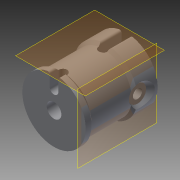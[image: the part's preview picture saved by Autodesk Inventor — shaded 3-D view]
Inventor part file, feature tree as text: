
AUTODESK INVENTOR PART (.ipt)
format: ipt  version: 2013 (Build 170138000, 138)  size: 317,952 bytes
history: native  units: in
note: dims shown in document units (in); Inventor stores cm internally (conversion verified against a paired STEP export)
features: extrude x13, sketch x13, pattern_circular x3, fillet x3, projected_geometry x3, chamfer x2, plane x2
ambient origin geometry x8: Origin, YZ Plane, XZ Plane, XY Plane, X Axis, Y Axis, Z Axis, Center Point
bodies: Solid1 (feature_tree)
feature tree (39):
  extrude  "Extrusion1"  Depth=0.9843in TaperAngle=0.0deg
  extrude  "Extrusion2"  Depth=0.315in TaperAngle=0.0deg
  extrude  "Extrusion3"  Depth=0.1181in TaperAngle=0.0deg
  chamfer  "Chamfer1"  Distance=0.0394in Angle=45.0deg
  extrude  "Extrusion4"  Depth=0.0984in
  extrude  "Extrusion5"  Depth=0.2008in
  plane  "Work Plane1"
  extrude  "Extrusion6"  Depth=0.1181in
  extrude  "Extrusion7"  Depth=0.1181in
  extrude  "Extrusion8"  Depth=0.1181in TaperAngle=0.0deg
  chamfer  "Chamfer2"  Distance=0.1181in
  extrude  "Extrusion9"  Depth=0.1575in
  extrude  "Extrusion10"  Depth=0.0394in
  pattern_circular  "Circular Pattern1"  Count=2 Angle=360.0deg
  fillet  "Fillet1"  Radius=0.0295in
  plane  "Work Plane2"
  extrude  "Extrusion15"  Depth=1.0in TaperAngle=0.0deg
  pattern_circular  "Circular Pattern3"  Angle=45.0deg  [1 undecoded]
  fillet  "Fillet3"  Radius=0.7874in
  extrude  "Extrusion11"  Depth=0.0394in
  extrude  "Extrusion14"  Depth=0.374in
  pattern_circular  "Circular Pattern2"  [2 undecoded]
  fillet  "Fillet2"  Radius=1.0in
  sketch  "Sketch1"  dims[d0=0.7874in d2=0.9843in d3=0.0in]
  sketch  "Sketch2"  dims[d4=0.0394in d5=0.315in d6=0.0in]
  sketch  "Sketch3"  dims[d7=0.0394in d8=0.1181in d9=0.0in d10=0.0394in d11=0.125in d12=45.0deg]
  sketch  "Sketch4"  dims[d14=0.126in d17=0.0984in]
  sketch  "Sketch5"  dims[d18=0.1181in d19=0.0in d20=0.2008in]
  sketch  "Sketch6"  dims[d22=0.2461in d23=0.1181in]
  projected_geometry  "Projected Loop1"
  sketch  "Sketch7"  dims[d24=0.1181in d25=0.0in d26=0.1181in]
  sketch  "Sketch8"  dims[d29=0.1181in d30=0.0in d31=0.1181in d32=0.0in d33=0.1181in d34=0.0in]
  sketch  "Sketch9"  dims[d35=0.0394in d36=0.125in d37=45.0deg d38=0.1575in]
  sketch  "Sketch10"  dims[d40=0.2205in d41=0.0394in]
  sketch  "Sketch11"  dims[d42=0.2165in d43=0.0in]
  sketch  "Sketch14"  dims[d44=0.2165in d45=0.0in d46=0.7874in d47=360.0deg d49=0.0295in]
  sketch  "Sketch15"  dims[d50=0.374in d51=1.0in d52=0.0in d57=1.0in d58=45.0deg d59=0.7874in d60=360.0deg d62=0.0394in d63=0.374in d64=0.2362in d66=1.0in d67=45.0deg d68=0.7874in d69=360.0deg d71=0.0394in]
  projected_geometry  "Project Cut Edges1"
  projected_geometry  "Project Cut Edges2"
note: 3 required parameter values undecoded (feature->parameter linkage not recoverable at this tier; creation-order binding heuristic only, values carry confidence <= 0.55)
